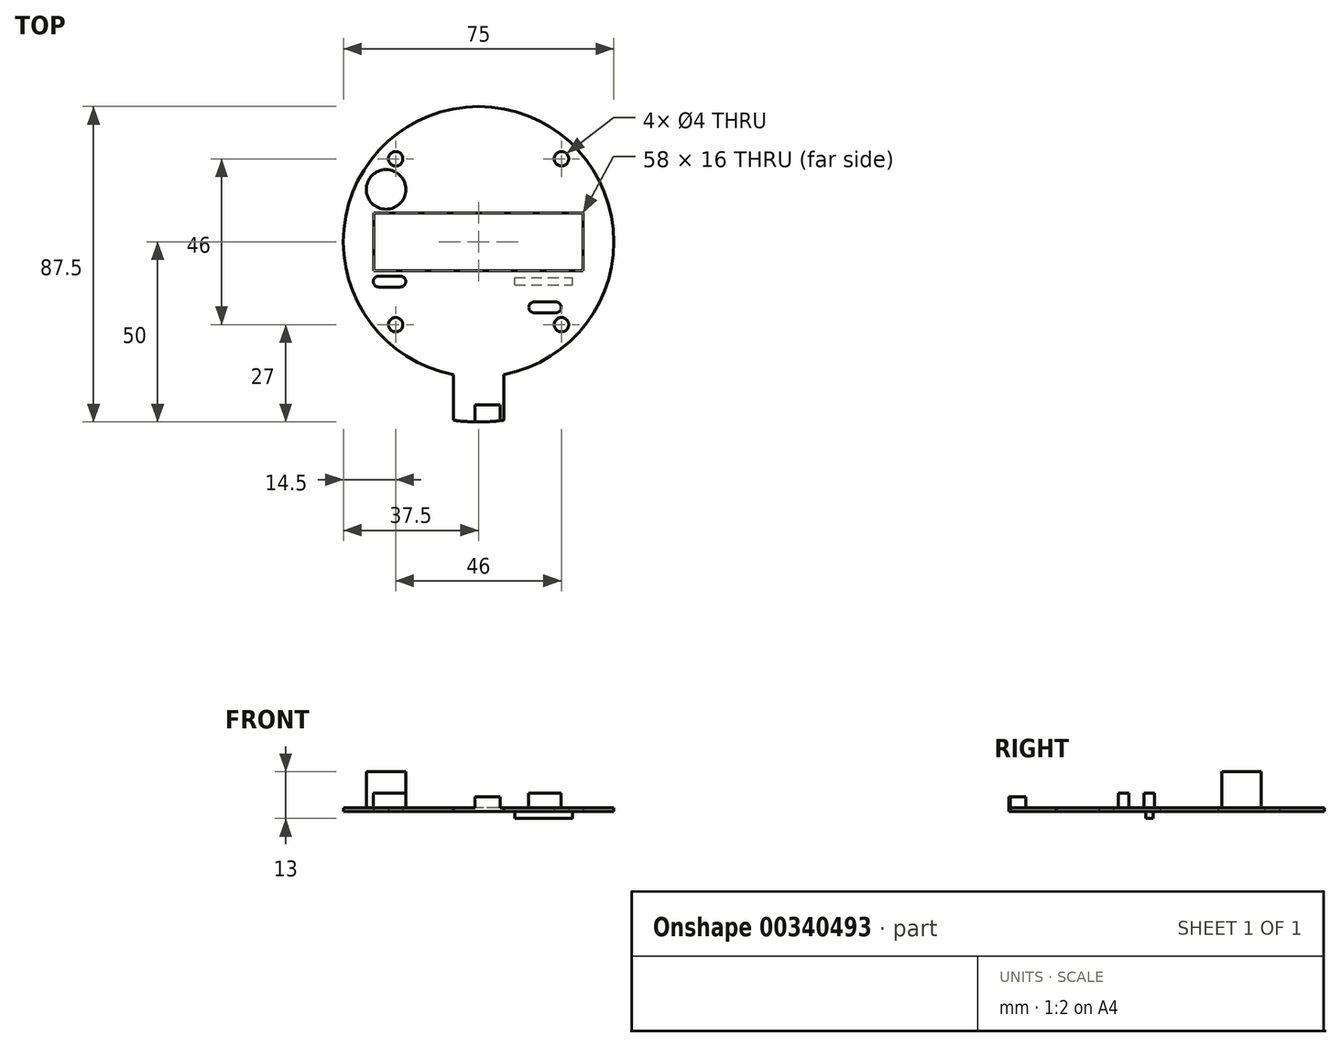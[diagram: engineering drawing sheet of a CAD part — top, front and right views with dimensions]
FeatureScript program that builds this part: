
annotation { "Feature Type Name" : "Feature", "Feature Type Description" : "" }
export const myFeature = defineFeature(function(context is Context, id is Id, definition is map)
    precondition{}
    {
        {
            var Q0;
            Q0=qCreatedBy(makeId("Top.planeOp"),FACE);
            var sketch = newSketch(context, id + "F0", { "sketchPlane" : qUnion([Q0])});
            skArc(sketch, "E0", {"start": v(7, -39.1) * mm, "mid": v(0, 35.24) * mm, "end": v(-7, -39.1) * mm});
            skArc(sketch, "E1", {"start": v(-7, -51.77) * mm, "mid": v(0, -52.26) * mm, "end": v(7, -51.77) * mm});
            skLineSegment(sketch, "E2.0", {"start": v(-7, -39.1) * mm, "end": v(-7, -52.26) * mm});
            skLineSegment(sketch, "E3.0", {"start": v(7, -39.1) * mm, "end": v(7, -52.26) * mm});
            skPoint(sketch, "E4.middle", {"position": v(0, 0) * mm});
            skLineSegment(sketch, "E5.bottom", {"start": v(29, -10.26) * mm, "end": v(-29, -10.26) * mm});
            skLineSegment(sketch, "E5.top", {"start": v(29, 5.74) * mm, "end": v(-29, 5.74) * mm});
            skLineSegment(sketch, "E5.left", {"start": v(29, -10.26) * mm, "end": v(29, 5.74) * mm});
            skLineSegment(sketch, "E5.right", {"start": v(-29, -10.26) * mm, "end": v(-29, 5.74) * mm});
            skCircle(sketch, "E6", {"center": v(-23, 20.74) * mm, "radius": 2 * mm});
            skCircle(sketch, "E7", {"center": v(23, 20.74) * mm, "radius": 2 * mm});
            skCircle(sketch, "E8", {"center": v(23, -25.26) * mm, "radius": 2 * mm});
            skCircle(sketch, "E9", {"center": v(-23, -25.26) * mm, "radius": 2 * mm});
            skSolve(sketch);
        }
        {
            var Q0;
            Q0=qSketchRegion(id+"F0",true);
            extrude(context, id + "F1", {"entities" : qUnion([Q0]), "depth" : 1 * mm});
        }
        {
            var Q0;
            Q0=makeQuery(id+"F1.opExtrude","CAP_FACE",FACE,{"disambiguationData":[OSD([sQuery(id+"F0.wireOp",EDGE,"E0"),sQuery(id+"F0.wireOp",EDGE,"E1"),sQuery(id+"F0.wireOp",EDGE,"E2.0"),sQuery(id+"F0.wireOp",EDGE,"E3.0"),sQuery(id+"F0.wireOp",EDGE,"E5.bottom"),sQuery(id+"F0.wireOp",EDGE,"E5.top"),sQuery(id+"F0.wireOp",EDGE,"E5.left"),sQuery(id+"F0.wireOp",EDGE,"E5.right"),sQuery(id+"F0.wireOp",EDGE,"E6"),sQuery(id+"F0.wireOp",EDGE,"E7"),sQuery(id+"F0.wireOp",EDGE,"E8"),sQuery(id+"F0.wireOp",EDGE,"E9")])],"isStart":false});
            var sketch = newSketch(context, id + "F2", { "sketchPlane" : qUnion([Q0])});
            skCircle(sketch, "E10", {"center": v(-25.64, 12.24) * mm, "radius": 5.5 * mm});
            skLineSegment(sketch, "E11.bottom", {"start": v(6, -52.52) * mm, "end": v(-1, -52.52) * mm});
            skLineSegment(sketch, "E11.top", {"start": v(6, -47.52) * mm, "end": v(-1, -47.52) * mm});
            skLineSegment(sketch, "E11.left", {"start": v(6, -52.52) * mm, "end": v(6, -47.52) * mm});
            skLineSegment(sketch, "E11.right", {"start": v(-1, -52.52) * mm, "end": v(-1, -47.52) * mm});
            skPoint(sketch, "E11.middle", {"position": v(2.5, -50.02) * mm});
            skLineSegment(sketch, "E12.bottom", {"start": v(-21.7, -14.83) * mm, "end": v(-27.7, -14.83) * mm});
            skLineSegment(sketch, "E12.top", {"start": v(-21.7, -11.83) * mm, "end": v(-27.7, -11.83) * mm});
            skPoint(sketch, "E12.middle", {"position": v(-24.7, -13.33) * mm});
            skArc(sketch, "E13", {"start": v(-27.7, -11.83) * mm, "mid": v(-29.2, -13.33) * mm, "end": v(-27.7, -14.83) * mm});
            skArc(sketch, "E14", {"start": v(-21.7, -14.83) * mm, "mid": v(-20.2, -13.33) * mm, "end": v(-21.7, -11.83) * mm});
            skLineSegment(sketch, "E15.bottom", {"start": v(21.43, -21.98) * mm, "end": v(15.43, -21.98) * mm});
            skLineSegment(sketch, "E15.top", {"start": v(21.43, -18.98) * mm, "end": v(15.43, -18.98) * mm});
            skArc(sketch, "E16", {"start": v(15.43, -18.98) * mm, "mid": v(13.93, -20.48) * mm, "end": v(15.43, -21.98) * mm});
            skArc(sketch, "E17", {"start": v(21.43, -21.98) * mm, "mid": v(22.93, -20.48) * mm, "end": v(21.43, -18.98) * mm});
            skSolve(sketch);
        }
        {
            var Q0;
            Q0=makeQuery(id+"F2.imprint","IMPRINT",FACE,{"disambiguationData":[TD([[makeQuery(id+"F2.imprint","IMPRINT",EDGE,{"derivedFrom":sQuery(id+"F2.wireOp",EDGE,"E10")}),1.0]])]});
            extrude(context, id + "F3", {"entities" : qUnion([Q0]), "operationType" : NewBodyOperationType.ADD, "depth" : 10 * mm});
        }
        {
            var Q0;
            Q0=makeQuery(id+"F2.imprint","IMPRINT",FACE,{"disambiguationData":[TD([[makeQuery(id+"F2.imprint","IMPRINT",EDGE,{"derivedFrom":sQuery(id+"F2.wireOp",EDGE,"E12.bottom")}),-1.0]])]});
            extrude(context, id + "F4", {"entities" : qUnion([Q0]), "operationType" : NewBodyOperationType.ADD, "depth" : 4 * mm});
        }
        {
            var Q0;
            Q0=makeQuery(id+"F2.imprint","IMPRINT",FACE,{"disambiguationData":[TD([[makeQuery(id+"F2.imprint","IMPRINT",EDGE,{"derivedFrom":sQuery(id+"F2.wireOp",EDGE,"E15.bottom")}),-1.0]])]});
            extrude(context, id + "F5", {"entities" : qUnion([Q0]), "operationType" : NewBodyOperationType.ADD, "depth" : 4 * mm});
        }
        {
            var Q0;
            {var subQ0=sQuery(id+"F2.wireOp",EDGE,"E11.top");Q0=makeQuery(id+"F2.imprint","IMPRINT",FACE,{"disambiguationData":[TD([[makeQuery(id+"F2.imprint","IMPRINT",EDGE,{"derivedFrom":subQ0}),1.0]])]});}
            extrude(context, id + "F6", {"entities" : qUnion([Q0]), "operationType" : NewBodyOperationType.ADD, "depth" : 3 * mm});
        }
        {
            var Q0;
            Q0=makeQuery(id+"F1.opExtrude","CAP_FACE",FACE,{"disambiguationData":[OSD([sQuery(id+"F0.wireOp",EDGE,"E0"),sQuery(id+"F0.wireOp",EDGE,"E1"),sQuery(id+"F0.wireOp",EDGE,"E2.0"),sQuery(id+"F0.wireOp",EDGE,"E3.0"),sQuery(id+"F0.wireOp",EDGE,"E5.bottom"),sQuery(id+"F0.wireOp",EDGE,"E5.top"),sQuery(id+"F0.wireOp",EDGE,"E5.left"),sQuery(id+"F0.wireOp",EDGE,"E5.right"),sQuery(id+"F0.wireOp",EDGE,"E6"),sQuery(id+"F0.wireOp",EDGE,"E7"),sQuery(id+"F0.wireOp",EDGE,"E8"),sQuery(id+"F0.wireOp",EDGE,"E9")])],"isStart":true});
            var sketch = newSketch(context, id + "F7", { "sketchPlane" : qUnion([Q0])});
            skLineSegment(sketch, "E18.bottom", {"start": v(10, 14.26) * mm, "end": v(26, 14.26) * mm});
            skLineSegment(sketch, "E18.top", {"start": v(10, 12.26) * mm, "end": v(26, 12.26) * mm});
            skLineSegment(sketch, "E18.left", {"start": v(10, 14.26) * mm, "end": v(10, 12.26) * mm});
            skLineSegment(sketch, "E18.right", {"start": v(26, 14.26) * mm, "end": v(26, 12.26) * mm});
            skSolve(sketch);
        }
        {
            var Q0;
            Q0=makeQuery(id+"F7.imprint","IMPRINT",FACE,{"disambiguationData":[TD([[makeQuery(id+"F7.imprint","IMPRINT",EDGE,{"derivedFrom":sQuery(id+"F7.wireOp",EDGE,"E18.bottom")}),-1.0]])]});
            extrude(context, id + "F8", {"entities" : qUnion([Q0]), "operationType" : NewBodyOperationType.ADD, "depth" : 2 * mm});
        }
    });
